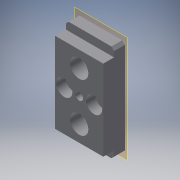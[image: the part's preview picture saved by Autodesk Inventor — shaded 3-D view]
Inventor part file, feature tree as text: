
AUTODESK INVENTOR PART (.ipt)
format: ipt  version: 2019.4 (Build 234330000, 330)  size: 223,232 bytes
history: native  units: mm
features: sketch x7, extrude x6, plane x4, reference x4, projected_geometry x4, other x4, hole x1
ambient origin geometry x8: Origin, YZ Plane, XZ Plane, XY Plane, X Axis, Y Axis, Z Axis, Center Point
bodies: Solid1 (feature_tree)
feature tree (30):
  plane  "Work Plane1"
  sketch  "Sketch1"  dims[d0=10.0mm d1=0.0mm d2=5.5mm]
  plane  "Work Plane2"
  plane  "Work Plane3"
  extrude  "Extrusion1"  Depth=10.0mm
  hole  "Hole1"  [1 undecoded]
  extrude  "Extrusion2"  Depth=10.0mm TaperAngle=0.0deg
  extrude  "Extrusion3"  Depth=7.8mm
  extrude  "Extrusion4"  Depth=1.5mm
  plane  "Work Plane4"
  extrude  "Extrusion5"  Depth=3.0mm
  extrude  "Extrusion6"  Depth=3.0mm
  reference  "Reference1"
  sketch  "Sketch2"  dims[d3=5.5mm]
  projected_geometry  "Projected Loop1"
  sketch  "Sketch3"  dims[d4=2.9mm d5=6.0mm d6=6.0mm d7=3.5mm d8=90.0deg d9=8.0mm d10=20.594885mm d11=6.75mm]
  reference  "Reference2"
  reference  "Reference3"
  sketch  "Sketch4"  dims[d12=6.75mm d13=10.0mm d14=0.0mm]
  sketch  "Sketch5"  dims[d15=7.8mm d16=7.8mm]
  reference  "Reference4"
  projected_geometry  "Projected Loop2"
  sketch  "Sketch6"  dims[d17=4.0mm d18=0.0mm d19=1.5mm]
  projected_geometry  "Projected Loop3"
  sketch  "Sketch7"  dims[d20=3.0mm d21=0.0mm d22=3.0mm d23=3.0mm d24=4.0mm d25=0.0mm d26=3.0mm d27=3.0mm d28=10.0mm d29=0.0mm]
  projected_geometry  "Projected Loop4"
  other  "Assembly_Omniscope_v1.iam"
  other  "01_Camera_Module_left_v0:1"
  other  "00_OV_lens:2"
  other  "00_OV_lens:1"
note: 1 required parameter value undecoded (feature->parameter linkage not recoverable at this tier; creation-order binding heuristic only, values carry confidence <= 0.55)
